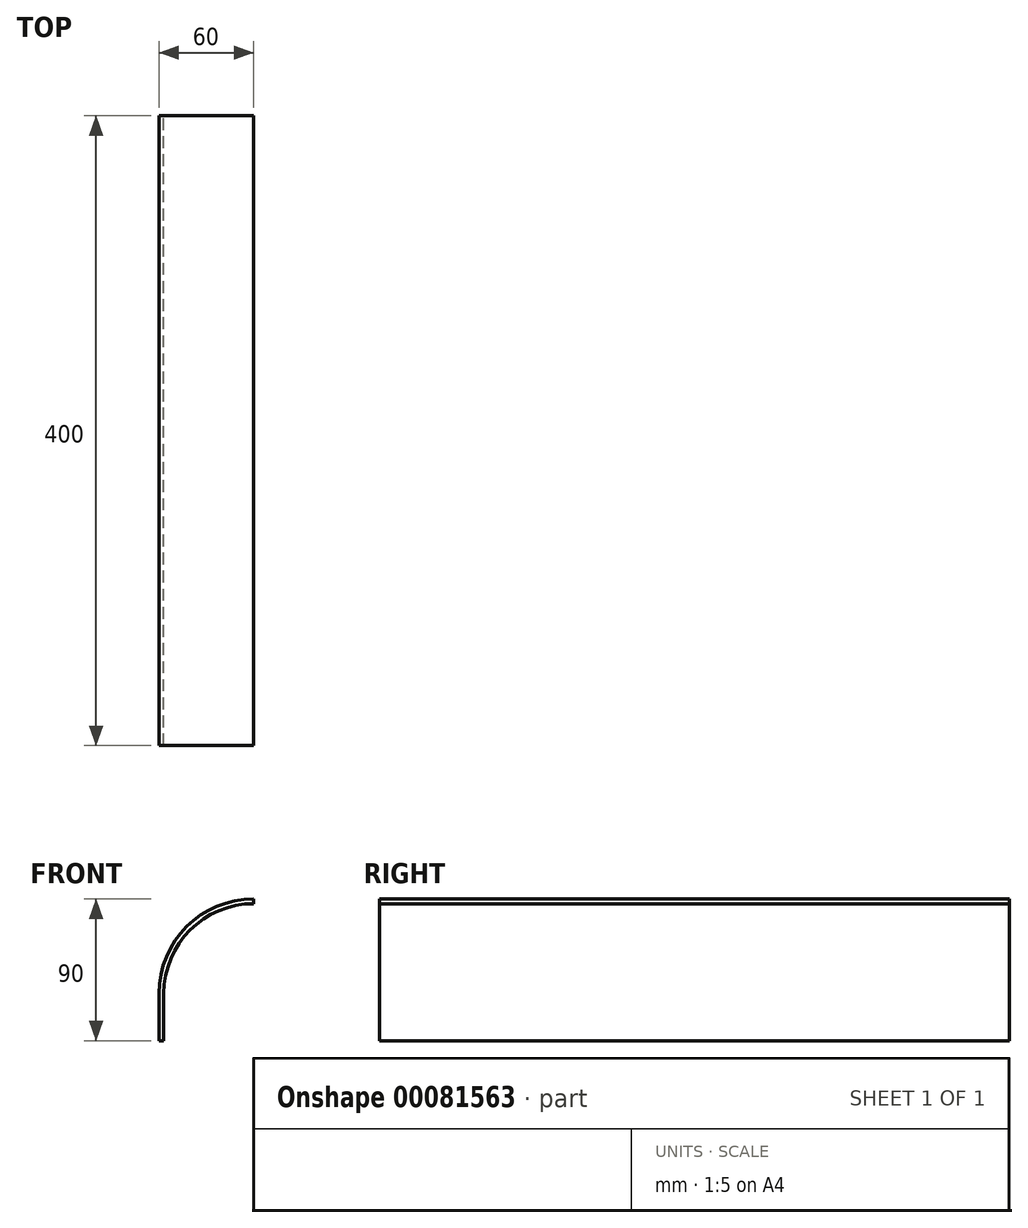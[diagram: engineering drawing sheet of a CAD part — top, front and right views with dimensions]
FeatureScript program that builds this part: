
annotation { "Feature Type Name" : "Feature", "Feature Type Description" : "" }
export const myFeature = defineFeature(function(context is Context, id is Id, definition is map)
    precondition{}
    {
        {
            var Q0;
            Q0=qCreatedBy(makeId("Front.planeOp"),FACE);
            var sketch = newSketch(context, id + "F0", { "sketchPlane" : qUnion([Q0])});
            skArc(sketch, "E0", {"start": v(-60, 0) * mm, "mid": v(-42.43, 42.43) * mm, "end": v(0, 60) * mm});
            skArc(sketch, "E1", {"start": v(-57, 0) * mm, "mid": v(-40.3, 40.3) * mm, "end": v(0, 57) * mm});
            skLineSegment(sketch, "E2", {"start": v(0, 57) * mm, "end": v(0, 60) * mm});
            skLineSegment(sketch, "E3", {"start": v(-60, 0) * mm, "end": v(-60, -30) * mm});
            skLineSegment(sketch, "E4", {"start": v(-60, -30) * mm, "end": v(-57, -30) * mm});
            skLineSegment(sketch, "E5", {"start": v(-57, -30) * mm, "end": v(-57, 0) * mm});
            skSolve(sketch);
        }
        {
            var Q0;
            Q0 = qSketchRegion(id + "F0", true);
            extrude(context, id + "F1", {"entities" : qUnion([Q0]), "depth" : 400 * mm});
        }
    });
